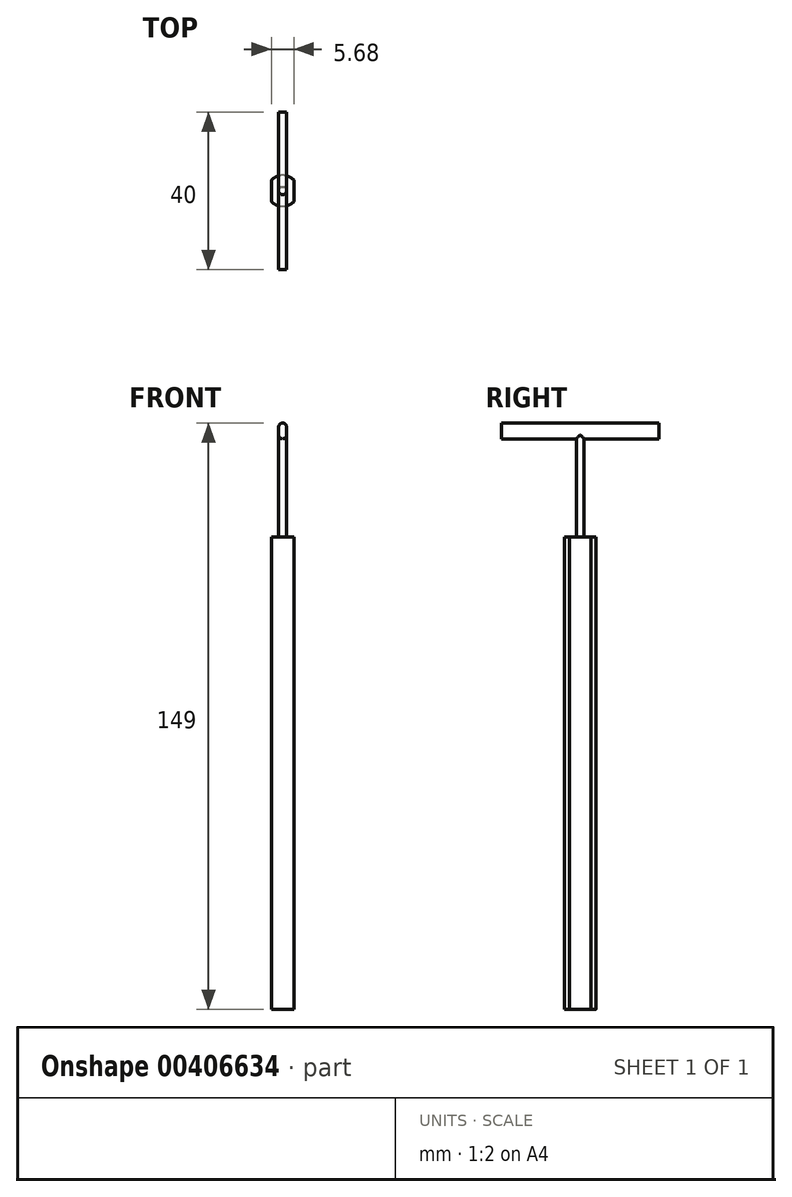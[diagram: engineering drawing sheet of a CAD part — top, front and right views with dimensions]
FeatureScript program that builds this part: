
annotation { "Feature Type Name" : "Feature", "Feature Type Description" : "" }
export const myFeature = defineFeature(function(context is Context, id is Id, definition is map)
    precondition{}
    {
        {
            var Q0;
            Q0=qCreatedBy(makeId("Top.planeOp"),FACE);
            var sketch = newSketch(context, id + "F0", { "sketchPlane" : qUnion([Q0])});
            skCircle(sketch, "E0", {"center": v(0, 0) * mm, "radius": 3.95 * mm});
            skSolve(sketch);
        }
        {
            var Q0;
            Q0 = qSketchRegion(id + "F0", true);
            extrude(context, id + "F1", {"entities" : qUnion([Q0]), "depth" : 120 * mm});
        }
        {
            var Q0;
            Q0=makeQuery(id+"F1.opExtrude","CAP_FACE",FACE,{"disambiguationData":[OSD([sQuery(id+"F0.wireOp",EDGE,"E0")])],"isStart":false});
            var sketch = newSketch(context, id + "F2", { "sketchPlane" : qUnion([Q0])});
            skLineSegment(sketch, "E1", {"start": v(-2.84, 2.75) * mm, "end": v(-2.84, -2.75) * mm});
            skLineSegment(sketch, "E2", {"start": v(2.84, 2.75) * mm, "end": v(2.84, -2.75) * mm});
            skSolve(sketch);
        }
        {
            var Q0;
            {var subQ0=sQuery(id+"F2.wireOp",EDGE,"E1");Q0=makeQuery(id+"F2.imprint","IMPRINT",FACE,{"disambiguationData":[TD([[makeQuery(id+"F2.imprint","IMPRINT",EDGE,{"derivedFrom":subQ0}),-1.0]])]});}
            var Q1;
            {var subQ0=sQuery(id+"F2.wireOp",EDGE,"E2");Q1=makeQuery(id+"F2.imprint","IMPRINT",FACE,{"disambiguationData":[TD([[makeQuery(id+"F2.imprint","IMPRINT",EDGE,{"derivedFrom":subQ0}),1.0]])]});}
            extrude(context, id + "F3", {"entities" : qUnion([Q0, Q1]), "operationType" : NewBodyOperationType.REMOVE, "endBound" : BoundingType.THROUGH_ALL, "oppositeDirection" : true, "depth" : 25 * mm});
        }
        {
            var Q0;
            Q0=makeQuery(id+"F1.opExtrude","CAP_FACE",FACE,{"disambiguationData":[OSD([sQuery(id+"F0.wireOp",EDGE,"E0")])],"isStart":false});
            var sketch = newSketch(context, id + "F4", { "sketchPlane" : qUnion([Q0])});
            skCircle(sketch, "E3", {"center": v(0, 0) * mm, "radius": 1 * mm});
            skSolve(sketch);
        }
        {
            var Q0;
            Q0 = qSketchRegion(id + "F4", true);
            extrude(context, id + "F5", {"entities" : qUnion([Q0]), "operationType" : NewBodyOperationType.ADD, "depth" : 25 * mm});
        }
        {
            var Q0;
            Q0=makeQuery(id+"F5.opExtrude","CAP_FACE",FACE,{"disambiguationData":[OSD([sQuery(id+"F4.wireOp",EDGE,"E3")])],"isStart":false});
            var sketch = newSketch(context, id + "F6", { "sketchPlane" : qUnion([Q0])});
            skLineSegment(sketch, "E4.bottom", {"start": v(1, -20) * mm, "end": v(-1, -20) * mm});
            skLineSegment(sketch, "E4.top", {"start": v(1, 20) * mm, "end": v(-1, 20) * mm});
            skLineSegment(sketch, "E4.left", {"start": v(1, -20) * mm, "end": v(1, 20) * mm});
            skLineSegment(sketch, "E4.right", {"start": v(-1, -20) * mm, "end": v(-1, 20) * mm});
            skPoint(sketch, "E4.middle", {"position": v(0, 0) * mm});
            skSolve(sketch);
        }
        {
            var Q0;
            Q0 = qSketchRegion(id + "F6", true);
            extrude(context, id + "F7", {"entities" : qUnion([Q0]), "operationType" : NewBodyOperationType.ADD, "depth" : 4 * mm});
        }
        {
            var Q0;
            Q0=makeQuery(id+"F7.opExtrude","CAP_EDGE",EDGE,{"disambiguationData":[OSD([sQuery(id+"F6.wireOp",EDGE,"E4.left")])],"isStart":false});
            var Q1;
            {var subQ0=sQuery(id+"F6.wireOp",EDGE,"E4.left");var subQ1=sQuery(id+"F6.wireOp",EDGE,"E4.bottom");Q1=makeQuery(id+"F7.boolean.opBoolean","SPLIT",EDGE,{"disambiguationData":[TD([makeQuery(id+"F7.opExtrude","SWEPT_FACE",FACE,{"disambiguationData":[OSD([subQ1])]})])],"derivedFrom":makeQuery(id+"F7.opExtrude","CAP_EDGE",EDGE,{"disambiguationData":[OSD([subQ0])],"isStart":true})});}
            var Q2;
            Q2=makeQuery(id+"F7.opExtrude","CAP_EDGE",EDGE,{"disambiguationData":[OSD([sQuery(id+"F6.wireOp",EDGE,"E4.right")])],"isStart":false});
            var Q3;
            {var subQ0=sQuery(id+"F6.wireOp",EDGE,"E4.right");var subQ1=sQuery(id+"F6.wireOp",EDGE,"E4.bottom");Q3=makeQuery(id+"F7.boolean.opBoolean","SPLIT",EDGE,{"disambiguationData":[TD([makeQuery(id+"F7.opExtrude","SWEPT_FACE",FACE,{"disambiguationData":[OSD([subQ1])]})])],"derivedFrom":makeQuery(id+"F7.opExtrude","CAP_EDGE",EDGE,{"disambiguationData":[OSD([subQ0])],"isStart":true})});}
            fillet(context, id + "F8", {"entities" : qUnion([Q0, Q1, Q2, Q3]), "radius" : 1 * mm, "tangentPropagation" : true, "allowEdgeOverflow" : false});
        }
    });
